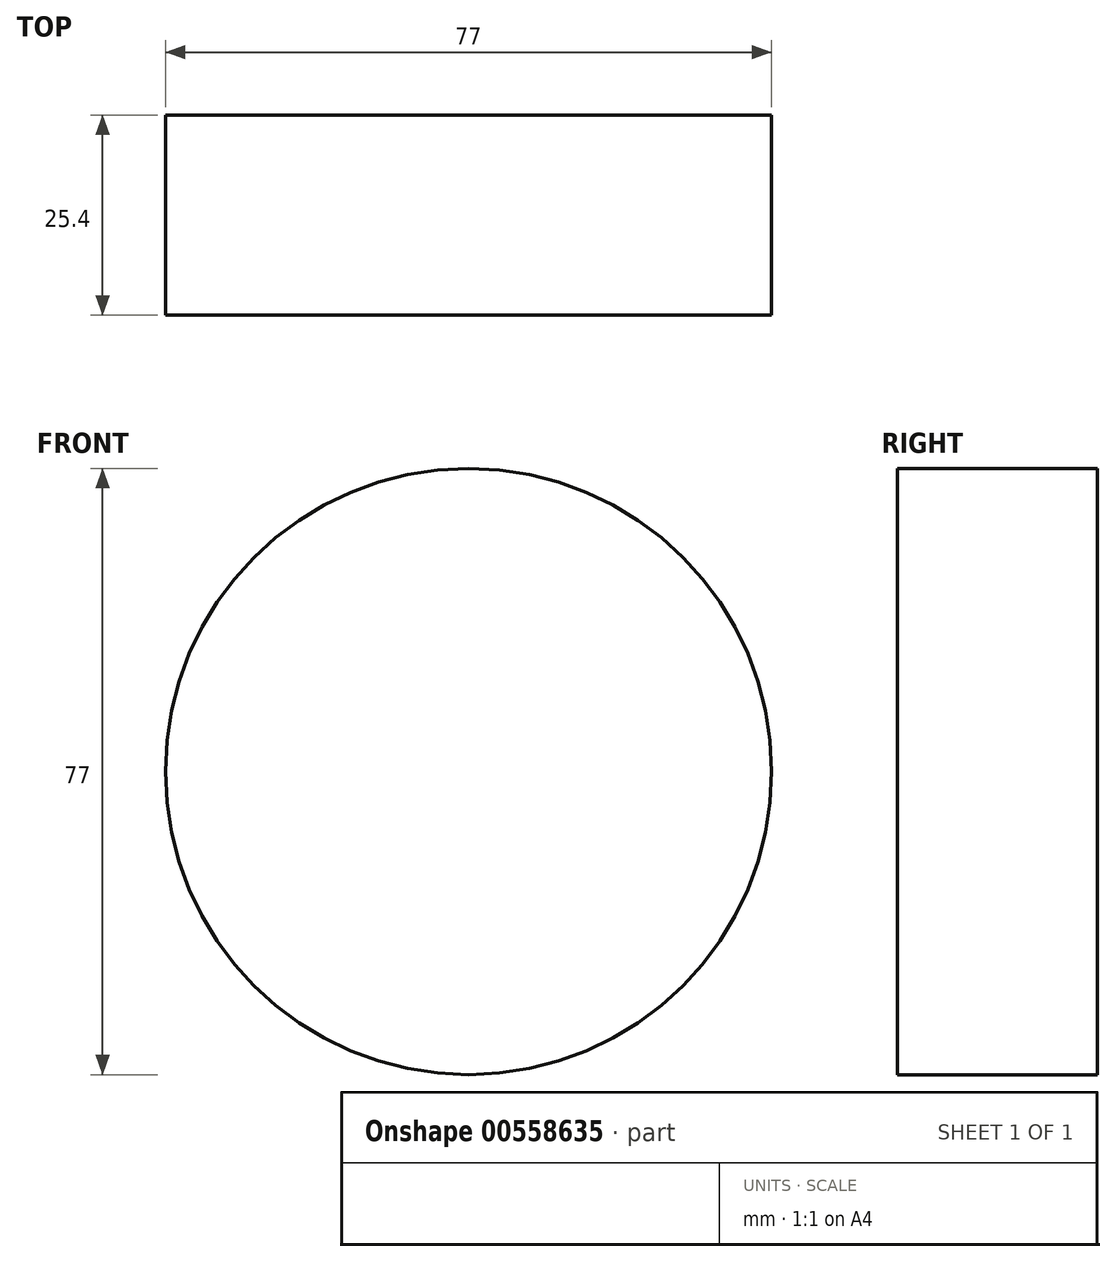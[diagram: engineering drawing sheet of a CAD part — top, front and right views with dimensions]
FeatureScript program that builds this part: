
annotation { "Feature Type Name" : "Feature", "Feature Type Description" : "" }
export const myFeature = defineFeature(function(context is Context, id is Id, definition is map)
    precondition{}
    {
        {
            var Q0;
            Q0=qCreatedBy(makeId("Front.planeOp"),FACE);
            var sketch = newSketch(context, id + "F0", { "sketchPlane" : qUnion([Q0])});
            skCircle(sketch, "E0", {"center": v(0, 0) * mm, "radius": 38.5 * mm});
            skSolve(sketch);
        }
        {
            var Q0;
            Q0 = qSketchRegion(id + "F0", true);
            extrude(context, id + "F1", {"entities" : qUnion([Q0]), "depth" : 25.4 * mm, "offsetDistance" : 25.4 * mm});
        }
    });
